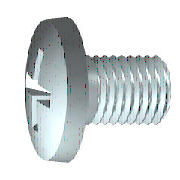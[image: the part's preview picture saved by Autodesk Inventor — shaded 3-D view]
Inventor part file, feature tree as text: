
AUTODESK INVENTOR PART (.ipt)
format: ipt  version: 2013 (Build 170138000, 138)  size: 243,712 bytes
history: native  units: mm (DEFAULTED — no unit token found)
features: other x2, extrude x1, plane x1
ambient origin geometry x7: Origin, YZ Plane, XZ Plane, X Axis, Y Axis, Z Axis, Center Point
bodies: Solid1 (feature_tree), Body (feature_tree)
feature tree (4):
  other  "IDS_WORKPLANE{1}"
  extrude  "Slot"  Depth=1.524mm
  other  "Cut"
  plane  "Work Plane3"
